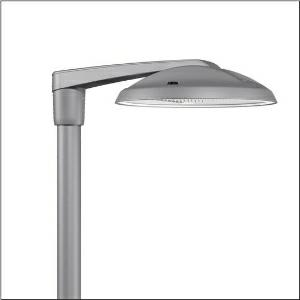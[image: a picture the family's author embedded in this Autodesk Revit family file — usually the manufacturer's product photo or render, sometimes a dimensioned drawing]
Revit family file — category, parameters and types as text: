
# Revit family: dl_r__50_iq_mini___st1_0a_5xa248d31v08ne_16c2
name_source: partatom
category: Lighting Fixtures
units: mm (PartAtom-declared; Revit-internal decimal feet)

## family parameters
Cut with Voids When Loaded = No
Host = Face
Light Source = No
Part Type = Normal
Room Calculation Point = No
Round Connector Dimension = Use Diameter
Shared = No

## types (1)
- --- (1 x LED, 17900 lm, 110.1 W, 3000K)
    Apparent Load = 110 VA
    CIE Flux Codes = 37 72 97 100 100
    Color Rendering = 70
    Color Temperature = 3000K
    Default Elevation = 1800 mm
    Description = DL® 50 iQ mini, mast luminaire, primary light control with lens, of PMMA, primary optical cover: cover, of toughened safety glass, transparent, light distribution: ST1.0a, light emission: direct distribution, primary light characteristic: asymmetric, installation type: post-top, side-entry, LED, High Power LED, rated luminous flux: 17.900lm, luminous efficacy: 163lm/W, light colour: 730, colour temperature: 3000K, control gear: iQ-Street Remote, D4i with power reduction, control: optimised constant luminous flux control (CLO 2.0), Desk-Remote (wireless, voltage-free reading and setting of iQ features in the workshop via application-optimized NFC function/RFID function), Light-Fading, Smart-Wire, Night-Set, Lumen-Switch, Temp-Guard, Auto-Match, Street-Remote, pre-setting: logarithmic dimming characteristic, mains connection: 230..240V, AC, 50/60Hz, connection cable pre-assembled, cable length: 10,5m, start of lifetime: 110W, end of service life: 116W, reduction: 50W, luminaire housing, of diecast aluminium, powder-coated, Siteco® metallic grey (DB 702S), inclination adjustable: 0°, 5°, 10° (post-top) | 0°, -5°, -10°, -15° (side-entry), please order mast post-top element or mast side-entry element separately, diameter: 500mm, height: 115mm, post-top: for spigot size d x l = 76 x 100mm; with reducer (optional accessory) 60 x 100mm | side-entry: for spigot size d x l = 60 x 100mm; with reducer (optional accessory) 42 x 100mm, mounting height: 4..6m, Smart Interface above, protection rating (complete): IP66, insulation class (complete): insulation class II (safety insulation), certification: CE, ENEC, ENEC+, VDE, impact resistance: IK08, permissible operating ambient temperature for outdoor applications: -25..+40°C, standard-compliant lighting for roads and squares, packaging unit: 1 piece

Light Distribution: ST1.0a
    Height = 115 mm
    Lamp = 1 x LED
    Lamp Light Flux = 17900 lm
    Lamp Power = 110.1 W
    Lamp count = 1
    Length = 500 mm
    Luminous efficacy = 163 lm/W
    Manufacturer = Siteco
    ModVariant = No
    Model = 5XA248D31V08NE
    Number of Poles = 1
    OnlyDefault = Yes
    Power Factor = 1
    Product Name = DL® 50 iQ mini | ST1.0a
    Product group = mast luminaire | pylon top
    ProductGroupID = 6100
    Protection Class = Protection class II
    Protection Degree = IP 66
    RLX_Detail_Level = 1
    RLX_Emergency_Light_Flux = 0 lm
    RLX_Emergency_Type = 0
    RLX_Emergency_Type_DB = No
    RlxData = <blob elided: 106921 chars, md5=ff051c90>
    Socket = socket
    Standby Power = 0 W
    System Light Flux = 17900 lm
    System Power = 110 W
    Type Comments = factory setting: luminous flux: 100 % | dim-lin: 254 | 601 mA
    Type Image = l_1251788.jpg
    URL = http://relux.com
    VarID = @adj_065514
    Voltage = 0 V
    Weight = 0.00 kg
    Width = 0 mm  [stored 0 ft]

note: [stored X ft] marks values corroborated as IEEE doubles in the binary element streams (Revit-internal decimal feet)

## geometry (parser evidence)
native form markers: Blend x4, Sweep x10
no freeform markers — native parametric forms only
